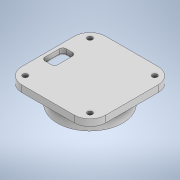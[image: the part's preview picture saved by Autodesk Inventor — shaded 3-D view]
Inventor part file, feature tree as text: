
AUTODESK INVENTOR PART (.ipt)
format: ipt  version: 2020 (Build 240168000, 168)  size: 481,792 bytes
history: native  units: mm
features: other x4, fillet x4, extrude x2, sketch x2
ambient origin geometry x8: Origin, YZ Plane, XZ Plane, XY Plane, X Axis, Y Axis, Z Axis, Center Point
bodies: Solid1 (feature_tree)
feature tree (12):
  other  "New Camera Board.ipt"
  extrude  "Extrusion1"  Depth=10.0mm
  fillet  "Fillet1"  Radius=32.2mm
  extrude  "Extrusion3"  Depth=1.0mm
  fillet  "Fillet2"  Radius=7.4mm
  fillet  "Fillet3"  Radius=9.4mm
  fillet  "Fillet4"  Radius=15.25mm
  other  "TaggingFeature1"
  sketch  "Sketch1"  dims[d0=10.0mm d1=31.028035mm d2=37.2mm d3=32.2mm d4=37.2mm]
  sketch  "Sketch2"  dims[d5=18.95mm d6=5.75mm d8=7.4mm d9=9.4mm d10=15.25mm d11=32.2mm d12=2.5mm d13=2.5mm d14=3.75mm d15=3.0mm d16=0.0mm d17=4.75mm d18=1.0mm d22=7.0mm d23=2.54mm d24=2.24mm d25=2.24mm d26=2.24mm d27=2.24mm d30=6.0mm d35=29.0mm d36=2.0mm d37=2.0mm d38=2.0mm d39=8.0mm d40=0.0mm d41=1.5mm d42=2.0mm d43=1.0mm]
  other  "Solid1::New Camera Board.ipt"
  other  "Srf1"
